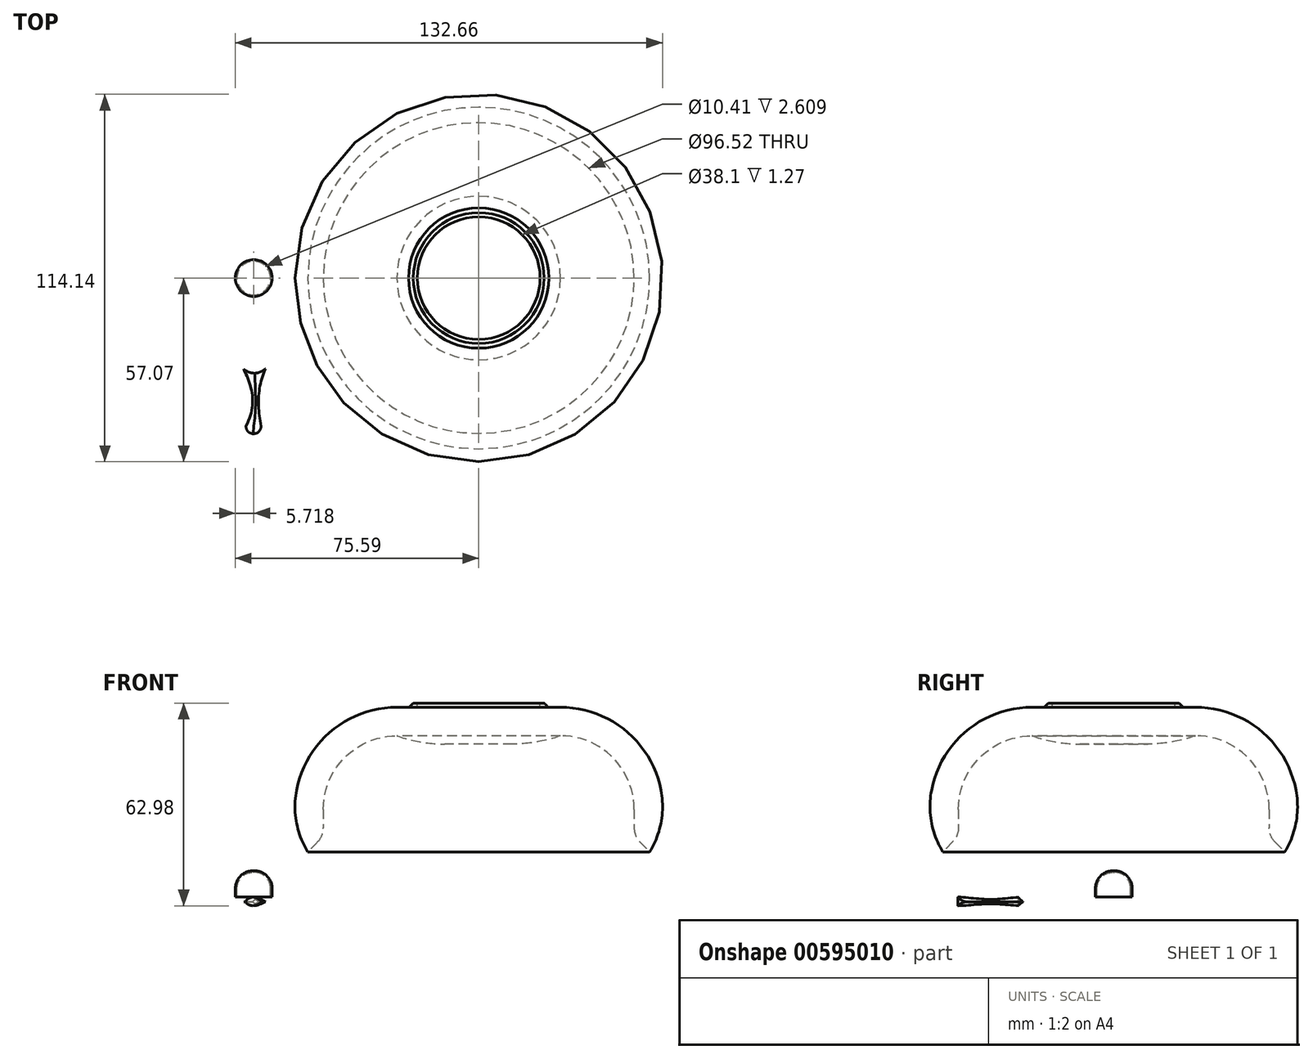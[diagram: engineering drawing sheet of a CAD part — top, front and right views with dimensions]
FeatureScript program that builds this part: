
annotation { "Feature Type Name" : "Feature", "Feature Type Description" : "" }
export const myFeature = defineFeature(function(context is Context, id is Id, definition is map)
    precondition{}
    {
        {
            var Q0;
            Q0=qCreatedBy(makeId("Top.planeOp"),FACE);
            var sketch = newSketch(context, id + "F0", { "sketchPlane" : qUnion([Q0])});
            skCircle(sketch, "E0", {"center": v(0, 0) * mm, "radius": 57.15 * mm});
            skSolve(sketch);
        }
        {
            var Q0;
            Q0=qSketchRegion(id+"F0",true);
            extrude(context, id + "F1", {"entities" : qUnion([Q0]), "depth" : 50.8 * mm, "offsetDistance" : 25.4 * mm});
        }
        {
            var Q0;
            Q0=makeQuery(id+"F1.opExtrude","CAP_EDGE",EDGE,{"disambiguationData":[OSD([sQuery(id+"F0.wireOp",EDGE,"E0")])],"isStart":false});
            fillet(context, id + "F2", {"entities" : qUnion([Q0]), "radius" : 31.75 * mm, "tangentPropagation" : true, "allowEdgeOverflow" : false});
        }
        {
            var Q0;
            Q0=makeQuery(id+"F1.opExtrude","CAP_FACE",FACE,{"disambiguationData":[OSD([sQuery(id+"F0.wireOp",EDGE,"E0")])],"isStart":true});
            shell(context, id + "F3", {"entities" : qUnion([Q0]), "thickness" : 8.9 * mm});
        }
        {
            var Q0;
            Q0=makeQuery(id+"F1.opExtrude","CAP_EDGE",EDGE,{"disambiguationData":[OSD([sQuery(id+"F0.wireOp",EDGE,"E0")])],"isStart":true});
            fillet(context, id + "F4", {"entities" : qUnion([Q0]), "radius" : 26.98 * mm, "tangentPropagation" : true, "allowEdgeOverflow" : false});
        }
        {
            var Q0;
            {var subQ0=sQuery(id+"F0.wireOp",EDGE,"E0");Q0=makeQuery(id+"F4.opFillet","BLEND_EDGE",EDGE,{"blendedFrom":[makeQuery(id+"F1.opExtrude","CAP_EDGE",EDGE,{"disambiguationData":[OSD([subQ0])],"isStart":true}),makeQuery(id+"F3.opShell","OFFSET_FACE",FACE,{"disambiguationData":[OSD([subQ0]),TDD([makeQuery(id+"F1.opExtrude","SWEPT_FACE",FACE,{"disambiguationData":[OSD([subQ0])]})])]})],"blendedInto":[makeQuery(id+"F3.opShell","OFFSET_FACE",FACE,{"disambiguationData":[OSD([subQ0]),TDD([makeQuery(id+"F1.opExtrude","SWEPT_FACE",FACE,{"disambiguationData":[OSD([subQ0])]})])]})]});}
            chamfer(context, id + "F5", {"entities" : qUnion([Q0]), "chamferType" : ChamferType.OFFSET_ANGLE, "width" : 6.35 * mm, "oppositeDirection" : false, "angle" : 45 * degree, "tangentPropagation" : true});
        }
        {
            var Q0;
            {var subQ0=sQuery(id+"F0.wireOp",EDGE,"E0");var subQ1=makeQuery(id+"F3.opShell","OFFSET_FACE",FACE,{"disambiguationData":[OSD([subQ0]),TDD([makeQuery(id+"F1.opExtrude","SWEPT_FACE",FACE,{"disambiguationData":[OSD([subQ0])]})])]});Q0=makeQuery(id+"F5.opChamfer","BLEND_EDGE",EDGE,{"blendedFrom":[makeQuery(id+"F4.opFillet","BLEND_EDGE",EDGE,{"blendedFrom":[makeQuery(id+"F1.opExtrude","CAP_EDGE",EDGE,{"disambiguationData":[OSD([subQ0])],"isStart":true}),subQ1],"blendedInto":[subQ1]}),subQ1],"blendedInto":[subQ1]});}
            chamfer(context, id + "F6", {"entities" : qUnion([Q0]), "width" : 5.08 * mm, "tangentPropagation" : true});
        }
        {
            var Q0;
            {var subQ0=sQuery(id+"F0.wireOp",EDGE,"E0");var subQ1=makeQuery(id+"F3.opShell","OFFSET_FACE",FACE,{"disambiguationData":[OSD([subQ0]),TDD([makeQuery(id+"F1.opExtrude","SWEPT_FACE",FACE,{"disambiguationData":[OSD([subQ0])]})])]});Q0=makeQuery(id+"F6.opChamfer","BLEND_EDGE",EDGE,{"blendedFrom":[makeQuery(id+"F5.opChamfer","BLEND_EDGE",EDGE,{"blendedFrom":[makeQuery(id+"F4.opFillet","BLEND_EDGE",EDGE,{"blendedFrom":[makeQuery(id+"F1.opExtrude","CAP_EDGE",EDGE,{"disambiguationData":[OSD([subQ0])],"isStart":true}),subQ1],"blendedInto":[subQ1]}),subQ1],"blendedInto":[subQ1]}),subQ1],"blendedInto":[subQ1]});}
            fillet(context, id + "F7", {"entities" : qUnion([Q0]), "radius" : 6.35 * mm, "tangentPropagation" : true, "allowEdgeOverflow" : false});
        }
        {
            var Q0;
            {var subQ0=sQuery(id+"F0.wireOp",EDGE,"E0");Q0=makeQuery(id+"F3.opShell","OFFSET_FACE",FACE,{"disambiguationData":[OSD([subQ0]),TDD([makeQuery(id+"F1.opExtrude","CAP_FACE",FACE,{"disambiguationData":[OSD([subQ0])],"isStart":false})])]});}
            extrude(context, id + "F8", {"entities" : qUnion([Q0]), "operationType" : NewBodyOperationType.ADD, "depth" : 2.54 * mm, "offsetDistance" : 25.4 * mm});
        }
        {
            var Q0;
            Q0=makeQuery(id+"F8.opExtrude","CAP_EDGE",EDGE,{"disambiguationData":[OSD([sQuery(id+"F0.wireOp",EDGE,"E0")])],"isStart":false});
            fillet(context, id + "F9", {"entities" : qUnion([Q0]), "radius" : 44.45 * mm, "tangentPropagation" : true, "allowEdgeOverflow" : false});
        }
        {
            var Q0;
            Q0=makeQuery(id+"F1.opExtrude","CAP_FACE",FACE,{"disambiguationData":[OSD([sQuery(id+"F0.wireOp",EDGE,"E0")])],"isStart":false});
            extrude(context, id + "F10", {"entities" : qUnion([Q0]), "operationType" : NewBodyOperationType.ADD, "depth" : 1.27 * mm, "offsetDistance" : 25.4 * mm});
        }
        {
            var Q0;
            Q0=makeQuery(id+"F10.opExtrude","CAP_EDGE",EDGE,{"disambiguationData":[OSD([sQuery(id+"F0.wireOp",EDGE,"E0")])],"isStart":false});
            chamfer(context, id + "F11", {"entities" : qUnion([Q0]), "width" : 5.08 * mm, "tangentPropagation" : true});
        }
        {
            var Q0;
            Q0=makeQuery(id+"F10.opExtrude","CAP_FACE",FACE,{"disambiguationData":[OSD([sQuery(id+"F0.wireOp",EDGE,"E0")])],"isStart":false});
            var sketch = newSketch(context, id + "F12", { "sketchPlane" : qUnion([Q0])});
            skCircle(sketch, "E1", {"center": v(0, 0) * mm, "radius": 19.05 * mm});
            skSolve(sketch);
        }
        {
            var Q0;
            Q0=makeQuery(id+"F12.imprint","IMPRINT",FACE,{"disambiguationData":[TD([[makeQuery(id+"F12.imprint","IMPRINT",EDGE,{"derivedFrom":sQuery(id+"F12.wireOp",EDGE,"E1")}),1.0]])]});
            extrude(context, id + "F13", {"entities" : qUnion([Q0]), "operationType" : NewBodyOperationType.REMOVE, "oppositeDirection" : true, "depth" : 1.27 * mm, "offsetDistance" : 25.4 * mm});
        }
        {
            var Q0;
            Q0=qCreatedBy(makeId("Top.planeOp"),FACE);
            var sketch = newSketch(context, id + "F14", { "sketchPlane" : qUnion([Q0])});
            skCircle(sketch, "E2", {"center": v(-69.87, 0) * mm, "radius": 5.72 * mm});
            skSolve(sketch);
        }
        {
            var Q0;
            Q0=makeQuery(id+"F14.imprint","IMPRINT",FACE,{"disambiguationData":[TD([[makeQuery(id+"F14.imprint","IMPRINT",EDGE,{"derivedFrom":sQuery(id+"F14.wireOp",EDGE,"E2")}),1.0]])]});
            extrude(context, id + "F15", {"entities" : qUnion([Q0]), "oppositeDirection" : true, "depth" : 8.13 * mm, "offsetDistance" : 25.4 * mm});
        }
        {
            var Q0;
            Q0=makeQuery(id+"F15.opExtrude","CAP_EDGE",EDGE,{"disambiguationData":[OSD([sQuery(id+"F14.wireOp",EDGE,"E2")])],"isStart":true});
            fillet(context, id + "F16", {"entities" : qUnion([Q0]), "radius" : 5.52 * mm, "tangentPropagation" : true, "allowEdgeOverflow" : false});
        }
        {
            var Q0;
            Q0=makeQuery(id+"F15.opExtrude","CAP_FACE",FACE,{"disambiguationData":[OSD([sQuery(id+"F14.wireOp",EDGE,"E2")])],"isStart":false});
            var sketch = newSketch(context, id + "F17", { "sketchPlane" : qUnion([Q0])});
            skCircle(sketch, "E3", {"center": v(-69.87, 0) * mm, "radius": 5.08 * mm});
            skFitSpline(sketch, "E4", {"points": [v(-66.2, 28.17) * mm, v(-67.62, 45.97) * mm], "startDerivative": vector(-8.12, 17.46) * mm, "endDerivative": vector(3.24, 18.24) * mm});
            skFitSpline(sketch, "E5", {"points": [v(-72.97, 28.4) * mm, v(-72.27, 45.97) * mm], "startDerivative": vector(8.3, 16.6) * mm, "endDerivative": vector(-10.3, 19.12) * mm});
            skArc(sketch, "E6", {"start": v(-67.62, 45.97) * mm, "mid": v(-69.95, 48.4) * mm, "end": v(-72.27, 45.97) * mm});
            skFitSpline(sketch, "E7", {"points": [v(-66.2, 28.17) * mm, v(-72.97, 28.4) * mm], "startDerivative": vector(-7.35, 5.9) * mm, "endDerivative": vector(-6.6, -4.42) * mm});
            skSolve(sketch);
        }
        {
            var Q0;
            Q0=makeQuery(id+"F15.opExtrude","CAP_FACE",FACE,{"disambiguationData":[OSD([sQuery(id+"F14.wireOp",EDGE,"E2")])],"isStart":false});
            shell(context, id + "F18", {"entities" : qUnion([Q0]), "thickness" : 0.5 * mm});
        }
        {
            var Q0;
            Q0=makeQuery(id+"F17.imprint","IMPRINT",FACE,{"disambiguationData":[TD([[makeQuery(id+"F17.imprint","IMPRINT",EDGE,{"derivedFrom":sQuery(id+"F17.wireOp",EDGE,"E4")}),1.0]])]});
            extrude(context, id + "F19", {"entities" : qUnion([Q0]), "depth" : 1.52 * mm, "offsetDistance" : 25.4 * mm});
        }
        {
            var Q0;
            Q0=makeQuery(id+"F19.opExtrude","CAP_EDGE",EDGE,{"disambiguationData":[OSD([sQuery(id+"F17.wireOp",EDGE,"E5")])],"isStart":true});
            var Q1;
            Q1=makeQuery(id+"F19.opExtrude","CAP_EDGE",EDGE,{"disambiguationData":[OSD([sQuery(id+"F17.wireOp",EDGE,"E4")])],"isStart":true});
            fillet(context, id + "F20", {"entities" : qUnion([Q0, Q1]), "radius" : 5.08 * mm, "tangentPropagation" : true, "allowEdgeOverflow" : false});
        }
        {
            var Q0;
            Q0=makeQuery(id+"F19.opExtrude","CAP_FACE",FACE,{"disambiguationData":[OSD([sQuery(id+"F17.wireOp",EDGE,"E4"),sQuery(id+"F17.wireOp",EDGE,"E5"),sQuery(id+"F17.wireOp",EDGE,"E6"),sQuery(id+"F17.wireOp",EDGE,"E7")])],"isStart":false});
            extrude(context, id + "F21", {"entities" : qUnion([Q0]), "operationType" : NewBodyOperationType.ADD, "depth" : 1.27 * mm, "offsetDistance" : 25.4 * mm});
        }
        {
            var Q0;
            {var subQ0=sQuery(id+"F17.wireOp",EDGE,"E7");var subQ1=sQuery(id+"F17.wireOp",EDGE,"E6");var subQ2=sQuery(id+"F17.wireOp",EDGE,"E5");var subQ3=sQuery(id+"F17.wireOp",EDGE,"E4");Q0=makeQuery(id+"F21.opExtrude","CAP_EDGE",EDGE,{"disambiguationData":[OSD([subQ3,subQ2,subQ1,subQ0]),TDD([makeQuery(id+"F20.opFillet","BLEND_EDGE",EDGE,{"blendedFrom":[makeQuery(id+"F19.opExtrude","CAP_EDGE",EDGE,{"disambiguationData":[OSD([subQ2])],"isStart":true}),makeQuery(id+"F19.opExtrude","CAP_FACE",FACE,{"disambiguationData":[OSD([subQ3,subQ2,subQ1,subQ0])],"isStart":false})],"blendedInto":[makeQuery(id+"F19.opExtrude","CAP_FACE",FACE,{"disambiguationData":[OSD([subQ3,subQ2,subQ1,subQ0])],"isStart":false})]})])],"isStart":false});}
            var Q1;
            {var subQ0=sQuery(id+"F17.wireOp",EDGE,"E7");var subQ1=sQuery(id+"F17.wireOp",EDGE,"E6");var subQ2=sQuery(id+"F17.wireOp",EDGE,"E5");var subQ3=sQuery(id+"F17.wireOp",EDGE,"E4");Q1=makeQuery(id+"F21.opExtrude","CAP_EDGE",EDGE,{"disambiguationData":[OSD([subQ3,subQ2,subQ1,subQ0]),TDD([makeQuery(id+"F20.opFillet","BLEND_EDGE",EDGE,{"blendedFrom":[makeQuery(id+"F19.opExtrude","CAP_EDGE",EDGE,{"disambiguationData":[OSD([subQ3])],"isStart":true}),makeQuery(id+"F19.opExtrude","CAP_FACE",FACE,{"disambiguationData":[OSD([subQ3,subQ2,subQ1,subQ0])],"isStart":false})],"blendedInto":[makeQuery(id+"F19.opExtrude","CAP_FACE",FACE,{"disambiguationData":[OSD([subQ3,subQ2,subQ1,subQ0])],"isStart":false})]})])],"isStart":false});}
            fillet(context, id + "F22", {"entities" : qUnion([Q0, Q1]), "radius" : 5.08 * mm, "tangentPropagation" : true, "allowEdgeOverflow" : false});
        }
    });
